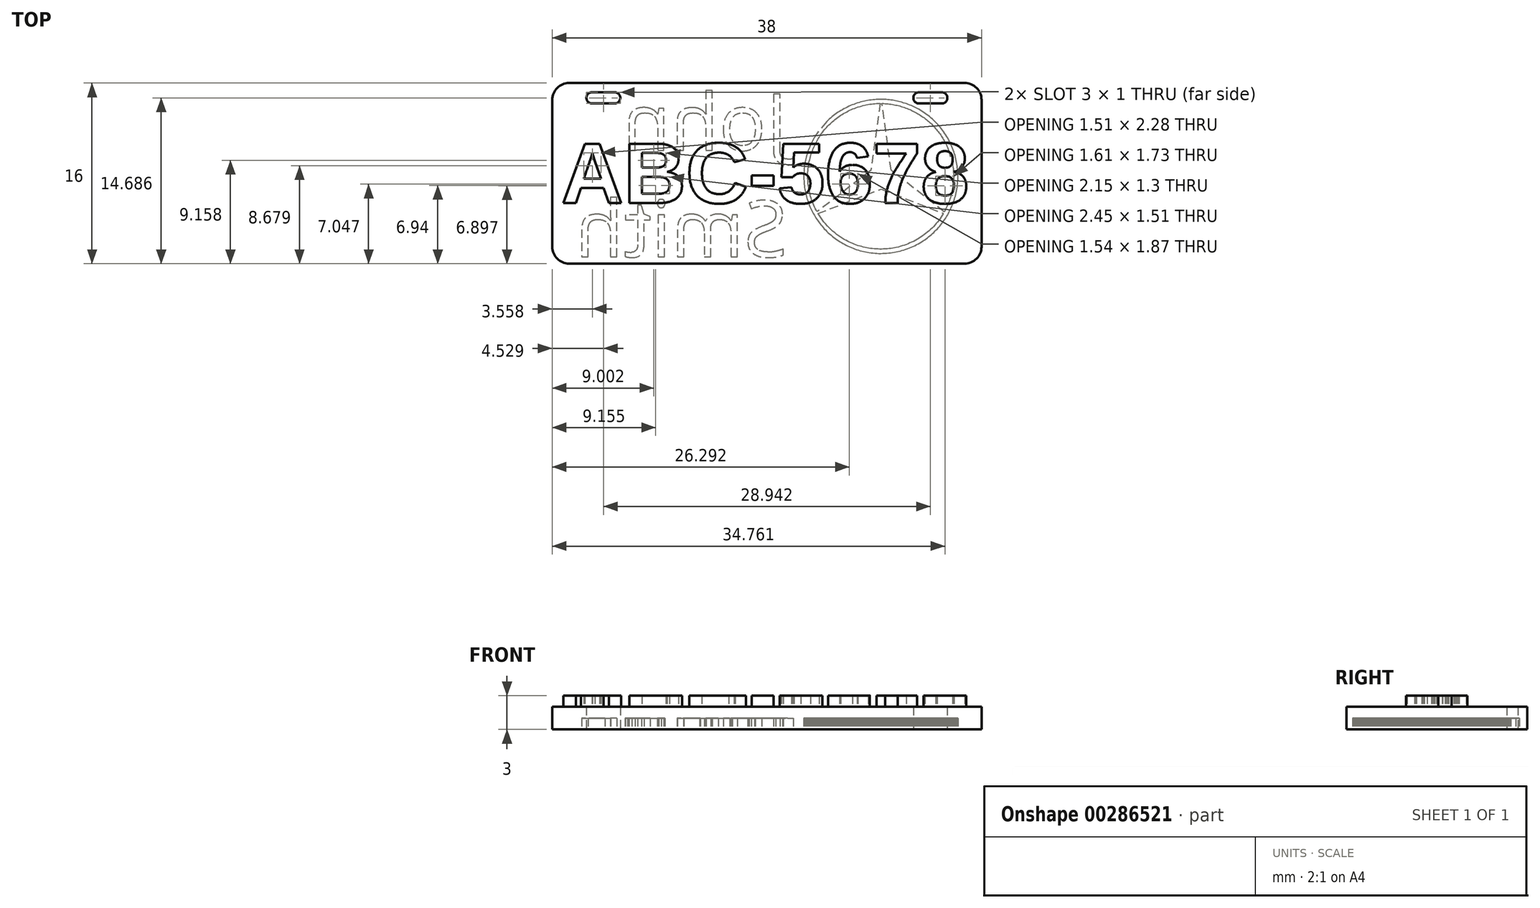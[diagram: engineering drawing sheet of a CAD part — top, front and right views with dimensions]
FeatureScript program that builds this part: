
annotation { "Feature Type Name" : "Feature", "Feature Type Description" : "" }
export const myFeature = defineFeature(function(context is Context, id is Id, definition is map)
    precondition{}
    {
        {
            var Q0;
            Q0=qCreatedBy(makeId("Top.planeOp"),FACE);
            var sketch = newSketch(context, id + "F0", { "sketchPlane" : qUnion([Q0])});
            skLineSegment(sketch, "E0.bottom", {"start": v(1.5, 0) * mm, "end": v(36.5, 0) * mm});
            skLineSegment(sketch, "E0.top", {"start": v(1.5, 16) * mm, "end": v(36.5, 16) * mm});
            skLineSegment(sketch, "E0.left", {"start": v(0, 1.5) * mm, "end": v(0, 14.5) * mm});
            skLineSegment(sketch, "E0.right", {"start": v(38, 1.5) * mm, "end": v(38, 14.5) * mm});
            skPoint(sketch, "E1.visualSharp", {"position": v(0, 16) * mm});
            skArc(sketch, "E1.filletArc", {"start": v(1.5, 16) * mm, "mid": v(0.44, 15.56) * mm, "end": v(0, 14.5) * mm});
            skPoint(sketch, "E2.visualSharp", {"position": v(38, 16) * mm});
            skArc(sketch, "E2.filletArc", {"start": v(38, 14.5) * mm, "mid": v(37.56, 15.56) * mm, "end": v(36.5, 16) * mm});
            skPoint(sketch, "E3.visualSharp", {"position": v(38, 0) * mm});
            skArc(sketch, "E3.filletArc", {"start": v(36.5, 0) * mm, "mid": v(37.56, 0.44) * mm, "end": v(38, 1.5) * mm});
            skPoint(sketch, "E4.visualSharp", {"position": v(0, 0) * mm});
            skArc(sketch, "E4.filletArc", {"start": v(0, 1.5) * mm, "mid": v(0.44, 0.44) * mm, "end": v(1.5, 0) * mm});
            skSolve(sketch);
        }
        {
            var Q0;
            Q0 = qSketchRegion(id + "F0", true);
            extrude(context, id + "F1", {"entities" : qUnion([Q0]), "depth" : 2 * mm, "offsetDistance" : 25 * mm});
        }
        {
            var Q0;
            Q0=makeQuery(id+"F1.opExtrude","CAP_FACE",FACE,{"disambiguationData":[OSD([sQuery(id+"F0.wireOp",EDGE,"E0.bottom"),sQuery(id+"F0.wireOp",EDGE,"E0.top"),sQuery(id+"F0.wireOp",EDGE,"E0.left"),sQuery(id+"F0.wireOp",EDGE,"E0.right"),sQuery(id+"F0.wireOp",EDGE,"E1.filletArc"),sQuery(id+"F0.wireOp",EDGE,"E2.filletArc"),sQuery(id+"F0.wireOp",EDGE,"E3.filletArc"),sQuery(id+"F0.wireOp",EDGE,"E4.filletArc")])],"isStart":false});
            var sketch = newSketch(context, id + "F2", { "sketchPlane" : qUnion([Q0])});
            skPoint(sketch, "E5", {"position": v(19, 16) * mm});
            skText(sketch, "E6", { "text": "ABC-5678", "fontName": "Arimo-Bold.ttf"});
            const initialGuessF2  = {"E6": [0.0008, 0.00537, 1, 0, 0.0055]};
            skSetInitialGuess(sketch, initialGuessF2);
            skSolve(sketch);
        }
        {
            var Q0;
            Q0 = qSketchRegion(id + "F2", true);
            extrude(context, id + "F3", {"entities" : qUnion([Q0]), "depth" : 1 * mm, "offsetDistance" : 25 * mm});
        }
        {
            var Q0;
            Q0=makeQuery(id+"F1.opExtrude","CAP_FACE",FACE,{"disambiguationData":[OSD([sQuery(id+"F0.wireOp",EDGE,"E0.bottom"),sQuery(id+"F0.wireOp",EDGE,"E0.top"),sQuery(id+"F0.wireOp",EDGE,"E0.left"),sQuery(id+"F0.wireOp",EDGE,"E0.right"),sQuery(id+"F0.wireOp",EDGE,"E1.filletArc"),sQuery(id+"F0.wireOp",EDGE,"E2.filletArc"),sQuery(id+"F0.wireOp",EDGE,"E3.filletArc"),sQuery(id+"F0.wireOp",EDGE,"E4.filletArc")])],"isStart":true});
            var sketch = newSketch(context, id + "F4", { "sketchPlane" : qUnion([Q0])});
            skLineSegment(sketch, "E7", {"start": v(32.84, -2.03) * mm, "end": v(32.96, -2.12) * mm});
            skLineSegment(sketch, "E8", {"start": v(32.96, -2.12) * mm, "end": v(33.09, -2.2) * mm});
            skLineSegment(sketch, "E9", {"start": v(33.09, -2.2) * mm, "end": v(33.2, -2.3) * mm});
            skLineSegment(sketch, "E10", {"start": v(33.2, -2.3) * mm, "end": v(33.32, -2.38) * mm});
            skLineSegment(sketch, "E11", {"start": v(33.32, -2.38) * mm, "end": v(33.44, -2.48) * mm});
            skLineSegment(sketch, "E12", {"start": v(33.44, -2.48) * mm, "end": v(33.55, -2.57) * mm});
            skLineSegment(sketch, "E13", {"start": v(33.55, -2.57) * mm, "end": v(33.67, -2.67) * mm});
            skLineSegment(sketch, "E14", {"start": v(33.67, -2.67) * mm, "end": v(33.78, -2.78) * mm});
            skLineSegment(sketch, "E15", {"start": v(33.78, -2.78) * mm, "end": v(33.88, -2.88) * mm});
            skLineSegment(sketch, "E16", {"start": v(33.88, -2.88) * mm, "end": v(33.99, -2.99) * mm});
            skLineSegment(sketch, "E17", {"start": v(33.99, -2.99) * mm, "end": v(34.1, -3.1) * mm});
            skLineSegment(sketch, "E18", {"start": v(34.1, -3.1) * mm, "end": v(34.2, -3.2) * mm});
            skLineSegment(sketch, "E19", {"start": v(34.2, -3.2) * mm, "end": v(34.3, -3.32) * mm});
            skLineSegment(sketch, "E20", {"start": v(34.3, -3.32) * mm, "end": v(34.39, -3.44) * mm});
            skLineSegment(sketch, "E21", {"start": v(34.39, -3.44) * mm, "end": v(34.48, -3.55) * mm});
            skLineSegment(sketch, "E22", {"start": v(34.48, -3.55) * mm, "end": v(34.57, -3.67) * mm});
            skLineSegment(sketch, "E23", {"start": v(34.57, -3.67) * mm, "end": v(34.66, -3.8) * mm});
            skLineSegment(sketch, "E24", {"start": v(34.66, -3.8) * mm, "end": v(34.74, -3.92) * mm});
            skLineSegment(sketch, "E25", {"start": v(34.74, -3.92) * mm, "end": v(34.82, -4.04) * mm});
            skLineSegment(sketch, "E26", {"start": v(34.82, -4.04) * mm, "end": v(34.9, -4.17) * mm});
            skLineSegment(sketch, "E27", {"start": v(34.9, -4.17) * mm, "end": v(34.98, -4.3) * mm});
            skLineSegment(sketch, "E28", {"start": v(34.98, -4.3) * mm, "end": v(35.05, -4.43) * mm});
            skLineSegment(sketch, "E29", {"start": v(35.05, -4.43) * mm, "end": v(35.12, -4.56) * mm});
            skLineSegment(sketch, "E30", {"start": v(35.12, -4.56) * mm, "end": v(35.2, -4.7) * mm});
            skLineSegment(sketch, "E31", {"start": v(35.2, -4.7) * mm, "end": v(35.26, -4.83) * mm});
            skLineSegment(sketch, "E32", {"start": v(35.26, -4.83) * mm, "end": v(35.32, -4.97) * mm});
            skLineSegment(sketch, "E33", {"start": v(35.32, -4.97) * mm, "end": v(35.38, -5.1) * mm});
            skLineSegment(sketch, "E34", {"start": v(35.38, -5.1) * mm, "end": v(35.44, -5.24) * mm});
            skLineSegment(sketch, "E35", {"start": v(35.44, -5.24) * mm, "end": v(35.49, -5.38) * mm});
            skLineSegment(sketch, "E36", {"start": v(35.49, -5.38) * mm, "end": v(35.54, -5.53) * mm});
            skLineSegment(sketch, "E37", {"start": v(35.54, -5.53) * mm, "end": v(35.6, -5.68) * mm});
            skLineSegment(sketch, "E38", {"start": v(35.6, -5.68) * mm, "end": v(35.64, -5.83) * mm});
            skLineSegment(sketch, "E39", {"start": v(35.64, -5.83) * mm, "end": v(35.68, -5.99) * mm});
            skLineSegment(sketch, "E40", {"start": v(35.68, -5.99) * mm, "end": v(35.72, -6.14) * mm});
            skLineSegment(sketch, "E41", {"start": v(35.72, -6.14) * mm, "end": v(35.76, -6.3) * mm});
            skLineSegment(sketch, "E42", {"start": v(35.76, -6.3) * mm, "end": v(35.79, -6.45) * mm});
            skLineSegment(sketch, "E43", {"start": v(35.79, -6.45) * mm, "end": v(35.81, -6.6) * mm});
            skLineSegment(sketch, "E44", {"start": v(35.81, -6.6) * mm, "end": v(35.84, -6.76) * mm});
            skLineSegment(sketch, "E45", {"start": v(35.84, -6.76) * mm, "end": v(35.86, -6.92) * mm});
            skLineSegment(sketch, "E46", {"start": v(35.86, -6.92) * mm, "end": v(35.88, -7.08) * mm});
            skLineSegment(sketch, "E47", {"start": v(35.88, -7.08) * mm, "end": v(35.89, -7.23) * mm});
            skLineSegment(sketch, "E48", {"start": v(35.89, -7.23) * mm, "end": v(35.9, -7.4) * mm});
            skLineSegment(sketch, "E49", {"start": v(35.9, -7.4) * mm, "end": v(35.9, -7.55) * mm});
            skLineSegment(sketch, "E50", {"start": v(35.9, -7.55) * mm, "end": v(35.9, -7.7) * mm});
            skLineSegment(sketch, "E51", {"start": v(35.9, -7.7) * mm, "end": v(35.9, -7.87) * mm});
            skLineSegment(sketch, "E52", {"start": v(35.9, -7.87) * mm, "end": v(35.9, -8.03) * mm});
            skLineSegment(sketch, "E53", {"start": v(35.9, -8.03) * mm, "end": v(35.9, -8.18) * mm});
            skLineSegment(sketch, "E54", {"start": v(35.9, -8.18) * mm, "end": v(35.88, -8.34) * mm});
            skLineSegment(sketch, "E55", {"start": v(35.88, -8.34) * mm, "end": v(35.86, -8.5) * mm});
            skLineSegment(sketch, "E56", {"start": v(35.86, -8.5) * mm, "end": v(35.84, -8.66) * mm});
            skLineSegment(sketch, "E57", {"start": v(35.84, -8.66) * mm, "end": v(35.82, -8.81) * mm});
            skLineSegment(sketch, "E58", {"start": v(35.82, -8.81) * mm, "end": v(35.8, -8.97) * mm});
            skLineSegment(sketch, "E59", {"start": v(35.8, -8.97) * mm, "end": v(35.76, -9.12) * mm});
            skLineSegment(sketch, "E60", {"start": v(35.76, -9.12) * mm, "end": v(35.73, -9.28) * mm});
            skLineSegment(sketch, "E61", {"start": v(35.73, -9.28) * mm, "end": v(35.69, -9.43) * mm});
            skLineSegment(sketch, "E62", {"start": v(35.69, -9.43) * mm, "end": v(35.65, -9.58) * mm});
            skLineSegment(sketch, "E63", {"start": v(35.65, -9.58) * mm, "end": v(35.6, -9.74) * mm});
            skLineSegment(sketch, "E64", {"start": v(35.6, -9.74) * mm, "end": v(35.55, -9.89) * mm});
            skLineSegment(sketch, "E65", {"start": v(35.55, -9.89) * mm, "end": v(35.5, -10.05) * mm});
            skLineSegment(sketch, "E66", {"start": v(35.5, -10.05) * mm, "end": v(35.44, -10.2) * mm});
            skLineSegment(sketch, "E67", {"start": v(35.44, -10.2) * mm, "end": v(35.38, -10.36) * mm});
            skLineSegment(sketch, "E68", {"start": v(35.38, -10.36) * mm, "end": v(35.31, -10.51) * mm});
            skLineSegment(sketch, "E69", {"start": v(35.31, -10.51) * mm, "end": v(35.24, -10.66) * mm});
            skLineSegment(sketch, "E70", {"start": v(35.24, -10.66) * mm, "end": v(35.17, -10.82) * mm});
            skLineSegment(sketch, "E71", {"start": v(35.17, -10.82) * mm, "end": v(35.1, -10.96) * mm});
            skLineSegment(sketch, "E72", {"start": v(35.1, -10.96) * mm, "end": v(35.01, -11.1) * mm});
            skLineSegment(sketch, "E73", {"start": v(35.01, -11.1) * mm, "end": v(34.93, -11.25) * mm});
            skLineSegment(sketch, "E74", {"start": v(34.93, -11.25) * mm, "end": v(34.84, -11.4) * mm});
            skLineSegment(sketch, "E75", {"start": v(34.84, -11.4) * mm, "end": v(34.75, -11.54) * mm});
            skLineSegment(sketch, "E76", {"start": v(34.75, -11.54) * mm, "end": v(34.65, -11.67) * mm});
            skLineSegment(sketch, "E77", {"start": v(34.65, -11.67) * mm, "end": v(34.55, -11.8) * mm});
            skLineSegment(sketch, "E78", {"start": v(34.55, -11.8) * mm, "end": v(34.45, -11.94) * mm});
            skLineSegment(sketch, "E79", {"start": v(34.45, -11.94) * mm, "end": v(34.34, -12.07) * mm});
            skLineSegment(sketch, "E80", {"start": v(34.34, -12.07) * mm, "end": v(34.24, -12.2) * mm});
            skLineSegment(sketch, "E81", {"start": v(34.24, -12.2) * mm, "end": v(34.12, -12.32) * mm});
            skLineSegment(sketch, "E82", {"start": v(34.12, -12.32) * mm, "end": v(34.01, -12.45) * mm});
            skLineSegment(sketch, "E83", {"start": v(34.01, -12.45) * mm, "end": v(33.9, -12.57) * mm});
            skLineSegment(sketch, "E84", {"start": v(33.9, -12.57) * mm, "end": v(33.77, -12.68) * mm});
            skLineSegment(sketch, "E85", {"start": v(33.77, -12.68) * mm, "end": v(33.65, -12.8) * mm});
            skLineSegment(sketch, "E86", {"start": v(33.65, -12.8) * mm, "end": v(33.52, -12.9) * mm});
            skLineSegment(sketch, "E87", {"start": v(33.52, -12.9) * mm, "end": v(33.4, -13.01) * mm});
            skLineSegment(sketch, "E88", {"start": v(33.4, -13.01) * mm, "end": v(33.27, -13.12) * mm});
            skLineSegment(sketch, "E89", {"start": v(33.27, -13.12) * mm, "end": v(33.13, -13.22) * mm});
            skLineSegment(sketch, "E90", {"start": v(33.13, -13.22) * mm, "end": v(33, -13.32) * mm});
            skLineSegment(sketch, "E91", {"start": v(33, -13.32) * mm, "end": v(32.86, -13.41) * mm});
            skLineSegment(sketch, "E92", {"start": v(32.86, -13.41) * mm, "end": v(32.72, -13.5) * mm});
            skLineSegment(sketch, "E93", {"start": v(32.72, -13.5) * mm, "end": v(32.57, -13.6) * mm});
            skLineSegment(sketch, "E94", {"start": v(32.57, -13.6) * mm, "end": v(32.42, -13.68) * mm});
            skLineSegment(sketch, "E95", {"start": v(32.42, -13.68) * mm, "end": v(32.3, -13.75) * mm});
            skLineSegment(sketch, "E96", {"start": v(32.3, -13.75) * mm, "end": v(32.17, -13.81) * mm});
            skLineSegment(sketch, "E97", {"start": v(32.17, -13.81) * mm, "end": v(32.04, -13.88) * mm});
            skLineSegment(sketch, "E98", {"start": v(32.04, -13.88) * mm, "end": v(31.9, -13.94) * mm});
            skLineSegment(sketch, "E99", {"start": v(31.9, -13.94) * mm, "end": v(31.78, -14) * mm});
            skLineSegment(sketch, "E100", {"start": v(31.78, -14) * mm, "end": v(31.64, -14.05) * mm});
            skLineSegment(sketch, "E101", {"start": v(31.64, -14.05) * mm, "end": v(31.5, -14.1) * mm});
            skLineSegment(sketch, "E102", {"start": v(31.5, -14.1) * mm, "end": v(31.37, -14.15) * mm});
            skLineSegment(sketch, "E103", {"start": v(31.37, -14.15) * mm, "end": v(31.24, -14.2) * mm});
            skLineSegment(sketch, "E104", {"start": v(31.24, -14.2) * mm, "end": v(31.1, -14.24) * mm});
            skLineSegment(sketch, "E105", {"start": v(31.1, -14.24) * mm, "end": v(30.96, -14.28) * mm});
            skLineSegment(sketch, "E106", {"start": v(30.96, -14.28) * mm, "end": v(30.82, -14.32) * mm});
            skLineSegment(sketch, "E107", {"start": v(30.82, -14.32) * mm, "end": v(30.68, -14.36) * mm});
            skLineSegment(sketch, "E108", {"start": v(30.68, -14.36) * mm, "end": v(30.54, -14.4) * mm});
            skLineSegment(sketch, "E109", {"start": v(30.54, -14.4) * mm, "end": v(30.4, -14.42) * mm});
            skLineSegment(sketch, "E110", {"start": v(30.4, -14.42) * mm, "end": v(30.26, -14.45) * mm});
            skLineSegment(sketch, "E111", {"start": v(30.26, -14.45) * mm, "end": v(30.12, -14.47) * mm});
            skLineSegment(sketch, "E112", {"start": v(30.12, -14.47) * mm, "end": v(29.98, -14.5) * mm});
            skLineSegment(sketch, "E113", {"start": v(29.98, -14.5) * mm, "end": v(29.84, -14.5) * mm});
            skLineSegment(sketch, "E114", {"start": v(29.84, -14.5) * mm, "end": v(29.7, -14.52) * mm});
            skLineSegment(sketch, "E115", {"start": v(29.7, -14.52) * mm, "end": v(29.55, -14.53) * mm});
            skLineSegment(sketch, "E116", {"start": v(29.55, -14.53) * mm, "end": v(29.4, -14.54) * mm});
            skLineSegment(sketch, "E117", {"start": v(29.4, -14.54) * mm, "end": v(29.26, -14.55) * mm});
            skLineSegment(sketch, "E118", {"start": v(29.26, -14.55) * mm, "end": v(29.12, -14.55) * mm});
            skLineSegment(sketch, "E119", {"start": v(29.12, -14.55) * mm, "end": v(28.97, -14.55) * mm});
            skLineSegment(sketch, "E120", {"start": v(28.97, -14.55) * mm, "end": v(28.83, -14.54) * mm});
            skLineSegment(sketch, "E121", {"start": v(28.83, -14.54) * mm, "end": v(28.69, -14.54) * mm});
            skLineSegment(sketch, "E122", {"start": v(28.69, -14.54) * mm, "end": v(28.54, -14.53) * mm});
            skLineSegment(sketch, "E123", {"start": v(28.54, -14.53) * mm, "end": v(28.4, -14.51) * mm});
            skLineSegment(sketch, "E124", {"start": v(28.4, -14.51) * mm, "end": v(28.24, -14.5) * mm});
            skLineSegment(sketch, "E125", {"start": v(28.24, -14.5) * mm, "end": v(28.08, -14.47) * mm});
            skLineSegment(sketch, "E126", {"start": v(28.08, -14.47) * mm, "end": v(27.93, -14.45) * mm});
            skLineSegment(sketch, "E127", {"start": v(27.93, -14.45) * mm, "end": v(27.77, -14.42) * mm});
            skLineSegment(sketch, "E128", {"start": v(27.77, -14.42) * mm, "end": v(27.61, -14.39) * mm});
            skLineSegment(sketch, "E129", {"start": v(27.61, -14.39) * mm, "end": v(27.46, -14.35) * mm});
            skLineSegment(sketch, "E130", {"start": v(27.46, -14.35) * mm, "end": v(27.3, -14.31) * mm});
            skLineSegment(sketch, "E131", {"start": v(27.3, -14.31) * mm, "end": v(27.15, -14.27) * mm});
            skLineSegment(sketch, "E132", {"start": v(27.15, -14.27) * mm, "end": v(27, -14.22) * mm});
            skLineSegment(sketch, "E133", {"start": v(27, -14.22) * mm, "end": v(26.85, -14.17) * mm});
            skLineSegment(sketch, "E134", {"start": v(26.85, -14.17) * mm, "end": v(26.7, -14.11) * mm});
            skLineSegment(sketch, "E135", {"start": v(26.7, -14.11) * mm, "end": v(26.55, -14.06) * mm});
            skLineSegment(sketch, "E136", {"start": v(26.55, -14.06) * mm, "end": v(26.4, -14) * mm});
            skLineSegment(sketch, "E137", {"start": v(26.4, -14) * mm, "end": v(26.25, -13.93) * mm});
            skLineSegment(sketch, "E138", {"start": v(26.25, -13.93) * mm, "end": v(26.1, -13.86) * mm});
            skLineSegment(sketch, "E139", {"start": v(26.1, -13.86) * mm, "end": v(25.97, -13.8) * mm});
            skLineSegment(sketch, "E140", {"start": v(25.97, -13.8) * mm, "end": v(25.83, -13.72) * mm});
            skLineSegment(sketch, "E141", {"start": v(25.83, -13.72) * mm, "end": v(25.69, -13.64) * mm});
            skLineSegment(sketch, "E142", {"start": v(25.69, -13.64) * mm, "end": v(25.55, -13.56) * mm});
            skLineSegment(sketch, "E143", {"start": v(25.55, -13.56) * mm, "end": v(25.41, -13.48) * mm});
            skLineSegment(sketch, "E144", {"start": v(25.41, -13.48) * mm, "end": v(25.28, -13.39) * mm});
            skLineSegment(sketch, "E145", {"start": v(25.28, -13.39) * mm, "end": v(25.15, -13.3) * mm});
            skLineSegment(sketch, "E146", {"start": v(25.15, -13.3) * mm, "end": v(25.02, -13.2) * mm});
            skLineSegment(sketch, "E147", {"start": v(25.02, -13.2) * mm, "end": v(24.9, -13.1) * mm});
            skLineSegment(sketch, "E148", {"start": v(24.9, -13.1) * mm, "end": v(24.77, -13) * mm});
            skLineSegment(sketch, "E149", {"start": v(24.77, -13) * mm, "end": v(24.65, -12.9) * mm});
            skLineSegment(sketch, "E150", {"start": v(24.65, -12.9) * mm, "end": v(24.53, -12.8) * mm});
            skLineSegment(sketch, "E151", {"start": v(24.53, -12.8) * mm, "end": v(24.4, -12.7) * mm});
            skLineSegment(sketch, "E152", {"start": v(24.4, -12.7) * mm, "end": v(24.3, -12.58) * mm});
            skLineSegment(sketch, "E153", {"start": v(24.3, -12.58) * mm, "end": v(23.55, -11.71) * mm});
            skLineSegment(sketch, "E154", {"start": v(23.55, -11.71) * mm, "end": v(23.22, -11.21) * mm});
            skLineSegment(sketch, "E155", {"start": v(23.22, -11.21) * mm, "end": v(23.12, -11.04) * mm});
            skLineSegment(sketch, "E156", {"start": v(23.12, -11.04) * mm, "end": v(23.05, -10.9) * mm});
            skLineSegment(sketch, "E157", {"start": v(23.05, -10.9) * mm, "end": v(22.99, -10.78) * mm});
            skLineSegment(sketch, "E158", {"start": v(22.99, -10.78) * mm, "end": v(22.92, -10.65) * mm});
            skLineSegment(sketch, "E159", {"start": v(22.92, -10.65) * mm, "end": v(22.87, -10.52) * mm});
            skLineSegment(sketch, "E160", {"start": v(22.87, -10.52) * mm, "end": v(22.8, -10.4) * mm});
            skLineSegment(sketch, "E161", {"start": v(22.8, -10.4) * mm, "end": v(22.75, -10.26) * mm});
            skLineSegment(sketch, "E162", {"start": v(22.75, -10.26) * mm, "end": v(22.7, -10.13) * mm});
            skLineSegment(sketch, "E163", {"start": v(22.7, -10.13) * mm, "end": v(22.65, -10) * mm});
            skLineSegment(sketch, "E164", {"start": v(22.65, -10) * mm, "end": v(22.6, -9.86) * mm});
            skLineSegment(sketch, "E165", {"start": v(22.6, -9.86) * mm, "end": v(22.57, -9.72) * mm});
            skLineSegment(sketch, "E166", {"start": v(22.57, -9.72) * mm, "end": v(22.52, -9.58) * mm});
            skLineSegment(sketch, "E167", {"start": v(22.52, -9.58) * mm, "end": v(22.49, -9.45) * mm});
            skLineSegment(sketch, "E168", {"start": v(22.49, -9.45) * mm, "end": v(22.45, -9.3) * mm});
            skLineSegment(sketch, "E169", {"start": v(22.45, -9.3) * mm, "end": v(22.42, -9.17) * mm});
            skLineSegment(sketch, "E170", {"start": v(22.42, -9.17) * mm, "end": v(22.4, -9.03) * mm});
            skLineSegment(sketch, "E171", {"start": v(22.4, -9.03) * mm, "end": v(22.37, -8.89) * mm});
            skLineSegment(sketch, "E172", {"start": v(22.37, -8.89) * mm, "end": v(22.34, -8.75) * mm});
            skLineSegment(sketch, "E173", {"start": v(22.34, -8.75) * mm, "end": v(22.32, -8.6) * mm});
            skLineSegment(sketch, "E174", {"start": v(22.32, -8.6) * mm, "end": v(22.3, -8.46) * mm});
            skLineSegment(sketch, "E175", {"start": v(22.3, -8.46) * mm, "end": v(22.3, -8.32) * mm});
            skLineSegment(sketch, "E176", {"start": v(22.3, -8.32) * mm, "end": v(22.28, -8.18) * mm});
            skLineSegment(sketch, "E177", {"start": v(22.28, -8.18) * mm, "end": v(22.27, -8.04) * mm});
            skLineSegment(sketch, "E178", {"start": v(22.27, -8.04) * mm, "end": v(22.27, -7.9) * mm});
            skLineSegment(sketch, "E179", {"start": v(22.27, -7.9) * mm, "end": v(22.27, -7.75) * mm});
            skLineSegment(sketch, "E180", {"start": v(22.27, -7.75) * mm, "end": v(22.27, -7.6) * mm});
            skLineSegment(sketch, "E181", {"start": v(22.27, -7.6) * mm, "end": v(22.27, -7.47) * mm});
            skLineSegment(sketch, "E182", {"start": v(22.27, -7.47) * mm, "end": v(22.28, -7.32) * mm});
            skLineSegment(sketch, "E183", {"start": v(22.28, -7.32) * mm, "end": v(22.29, -7.18) * mm});
            skLineSegment(sketch, "E184", {"start": v(22.29, -7.18) * mm, "end": v(22.3, -7.04) * mm});
            skLineSegment(sketch, "E185", {"start": v(22.3, -7.04) * mm, "end": v(22.32, -6.9) * mm});
            skLineSegment(sketch, "E186", {"start": v(22.32, -6.9) * mm, "end": v(22.34, -6.75) * mm});
            skLineSegment(sketch, "E187", {"start": v(22.34, -6.75) * mm, "end": v(22.36, -6.6) * mm});
            skLineSegment(sketch, "E188", {"start": v(22.36, -6.6) * mm, "end": v(22.39, -6.46) * mm});
            skLineSegment(sketch, "E189", {"start": v(22.39, -6.46) * mm, "end": v(22.41, -6.32) * mm});
            skLineSegment(sketch, "E190", {"start": v(22.41, -6.32) * mm, "end": v(22.45, -6.18) * mm});
            skLineSegment(sketch, "E191", {"start": v(22.45, -6.18) * mm, "end": v(22.48, -6.03) * mm});
            skLineSegment(sketch, "E192", {"start": v(22.48, -6.03) * mm, "end": v(22.52, -5.9) * mm});
            skLineSegment(sketch, "E193", {"start": v(22.52, -5.9) * mm, "end": v(22.56, -5.75) * mm});
            skLineSegment(sketch, "E194", {"start": v(22.56, -5.75) * mm, "end": v(22.6, -5.61) * mm});
            skLineSegment(sketch, "E195", {"start": v(22.6, -5.61) * mm, "end": v(22.65, -5.47) * mm});
            skLineSegment(sketch, "E196", {"start": v(22.65, -5.47) * mm, "end": v(22.7, -5.34) * mm});
            skLineSegment(sketch, "E197", {"start": v(22.7, -5.34) * mm, "end": v(22.75, -5.2) * mm});
            skLineSegment(sketch, "E198", {"start": v(22.75, -5.2) * mm, "end": v(22.8, -5.07) * mm});
            skLineSegment(sketch, "E199", {"start": v(22.8, -5.07) * mm, "end": v(22.87, -4.93) * mm});
            skLineSegment(sketch, "E200", {"start": v(22.87, -4.93) * mm, "end": v(22.93, -4.8) * mm});
            skLineSegment(sketch, "E201", {"start": v(22.93, -4.8) * mm, "end": v(23, -4.67) * mm});
            skLineSegment(sketch, "E202", {"start": v(23, -4.67) * mm, "end": v(23.06, -4.54) * mm});
            skLineSegment(sketch, "E203", {"start": v(23.06, -4.54) * mm, "end": v(23.13, -4.4) * mm});
            skLineSegment(sketch, "E204", {"start": v(23.13, -4.4) * mm, "end": v(23.2, -4.28) * mm});
            skLineSegment(sketch, "E205", {"start": v(23.2, -4.28) * mm, "end": v(23.28, -4.16) * mm});
            skLineSegment(sketch, "E206", {"start": v(23.28, -4.16) * mm, "end": v(23.35, -4.03) * mm});
            skLineSegment(sketch, "E207", {"start": v(23.35, -4.03) * mm, "end": v(23.43, -3.91) * mm});
            skLineSegment(sketch, "E208", {"start": v(23.43, -3.91) * mm, "end": v(23.52, -3.8) * mm});
            skLineSegment(sketch, "E209", {"start": v(23.52, -3.8) * mm, "end": v(23.6, -3.67) * mm});
            skLineSegment(sketch, "E210", {"start": v(23.6, -3.67) * mm, "end": v(23.7, -3.56) * mm});
            skLineSegment(sketch, "E211", {"start": v(23.7, -3.56) * mm, "end": v(23.78, -3.44) * mm});
            skLineSegment(sketch, "E212", {"start": v(23.78, -3.44) * mm, "end": v(23.87, -3.33) * mm});
            skLineSegment(sketch, "E213", {"start": v(23.87, -3.33) * mm, "end": v(23.97, -3.22) * mm});
            skLineSegment(sketch, "E214", {"start": v(23.97, -3.22) * mm, "end": v(24.08, -3.1) * mm});
            skLineSegment(sketch, "E215", {"start": v(24.08, -3.1) * mm, "end": v(24.2, -2.98) * mm});
            skLineSegment(sketch, "E216", {"start": v(24.2, -2.98) * mm, "end": v(24.3, -2.86) * mm});
            skLineSegment(sketch, "E217", {"start": v(24.3, -2.86) * mm, "end": v(24.43, -2.75) * mm});
            skLineSegment(sketch, "E218", {"start": v(24.43, -2.75) * mm, "end": v(24.55, -2.64) * mm});
            skLineSegment(sketch, "E219", {"start": v(24.55, -2.64) * mm, "end": v(24.67, -2.53) * mm});
            skLineSegment(sketch, "E220", {"start": v(24.67, -2.53) * mm, "end": v(24.8, -2.43) * mm});
            skLineSegment(sketch, "E221", {"start": v(24.8, -2.43) * mm, "end": v(24.93, -2.33) * mm});
            skLineSegment(sketch, "E222", {"start": v(24.93, -2.33) * mm, "end": v(25.06, -2.23) * mm});
            skLineSegment(sketch, "E223", {"start": v(25.06, -2.23) * mm, "end": v(25.19, -2.13) * mm});
            skLineSegment(sketch, "E224", {"start": v(25.19, -2.13) * mm, "end": v(25.33, -2.04) * mm});
            skLineSegment(sketch, "E225", {"start": v(25.33, -2.04) * mm, "end": v(25.46, -1.95) * mm});
            skLineSegment(sketch, "E226", {"start": v(25.46, -1.95) * mm, "end": v(25.6, -1.87) * mm});
            skLineSegment(sketch, "E227", {"start": v(25.6, -1.87) * mm, "end": v(25.74, -1.79) * mm});
            skLineSegment(sketch, "E228", {"start": v(25.74, -1.79) * mm, "end": v(25.89, -1.7) * mm});
            skLineSegment(sketch, "E229", {"start": v(25.89, -1.7) * mm, "end": v(26.03, -1.63) * mm});
            skLineSegment(sketch, "E230", {"start": v(26.03, -1.63) * mm, "end": v(26.18, -1.56) * mm});
            skLineSegment(sketch, "E231", {"start": v(26.18, -1.56) * mm, "end": v(26.33, -1.5) * mm});
            skLineSegment(sketch, "E232", {"start": v(26.33, -1.5) * mm, "end": v(26.48, -1.43) * mm});
            skLineSegment(sketch, "E233", {"start": v(26.48, -1.43) * mm, "end": v(26.63, -1.37) * mm});
            skLineSegment(sketch, "E234", {"start": v(26.63, -1.37) * mm, "end": v(26.78, -1.3) * mm});
            skLineSegment(sketch, "E235", {"start": v(26.78, -1.3) * mm, "end": v(26.94, -1.26) * mm});
            skLineSegment(sketch, "E236", {"start": v(26.94, -1.26) * mm, "end": v(27.1, -1.2) * mm});
            skLineSegment(sketch, "E237", {"start": v(27.1, -1.2) * mm, "end": v(27.25, -1.16) * mm});
            skLineSegment(sketch, "E238", {"start": v(27.25, -1.16) * mm, "end": v(27.41, -1.12) * mm});
            skLineSegment(sketch, "E239", {"start": v(27.41, -1.12) * mm, "end": v(27.57, -1.08) * mm});
            skLineSegment(sketch, "E240", {"start": v(27.57, -1.08) * mm, "end": v(27.73, -1.04) * mm});
            skLineSegment(sketch, "E241", {"start": v(27.73, -1.04) * mm, "end": v(27.9, -1.01) * mm});
            skLineSegment(sketch, "E242", {"start": v(27.9, -1.01) * mm, "end": v(28.05, -0.99) * mm});
            skLineSegment(sketch, "E243", {"start": v(28.05, -0.99) * mm, "end": v(28.22, -0.96) * mm});
            skLineSegment(sketch, "E244", {"start": v(28.22, -0.96) * mm, "end": v(28.4, -0.94) * mm});
            skLineSegment(sketch, "E245", {"start": v(28.4, -0.94) * mm, "end": v(28.57, -0.93) * mm});
            skLineSegment(sketch, "E246", {"start": v(28.57, -0.93) * mm, "end": v(28.74, -0.92) * mm});
            skLineSegment(sketch, "E247", {"start": v(28.74, -0.92) * mm, "end": v(28.91, -0.9) * mm});
            skLineSegment(sketch, "E248", {"start": v(28.91, -0.9) * mm, "end": v(29.08, -0.9) * mm});
            skLineSegment(sketch, "E249", {"start": v(29.08, -0.9) * mm, "end": v(29.26, -0.91) * mm});
            skLineSegment(sketch, "E250", {"start": v(29.26, -0.91) * mm, "end": v(29.43, -0.92) * mm});
            skLineSegment(sketch, "E251", {"start": v(29.43, -0.92) * mm, "end": v(29.6, -0.93) * mm});
            skLineSegment(sketch, "E252", {"start": v(29.6, -0.93) * mm, "end": v(29.77, -0.94) * mm});
            skLineSegment(sketch, "E253", {"start": v(29.77, -0.94) * mm, "end": v(29.95, -0.96) * mm});
            skLineSegment(sketch, "E254", {"start": v(29.95, -0.96) * mm, "end": v(30.12, -0.99) * mm});
            skLineSegment(sketch, "E255", {"start": v(30.12, -0.99) * mm, "end": v(30.29, -1.02) * mm});
            skLineSegment(sketch, "E256", {"start": v(30.29, -1.02) * mm, "end": v(30.46, -1.05) * mm});
            skLineSegment(sketch, "E257", {"start": v(30.46, -1.05) * mm, "end": v(30.63, -1.09) * mm});
            skLineSegment(sketch, "E258", {"start": v(30.63, -1.09) * mm, "end": v(30.8, -1.13) * mm});
            skLineSegment(sketch, "E259", {"start": v(30.8, -1.13) * mm, "end": v(30.96, -1.17) * mm});
            skLineSegment(sketch, "E260", {"start": v(30.96, -1.17) * mm, "end": v(31.13, -1.22) * mm});
            skLineSegment(sketch, "E261", {"start": v(31.13, -1.22) * mm, "end": v(31.3, -1.28) * mm});
            skLineSegment(sketch, "E262", {"start": v(31.3, -1.28) * mm, "end": v(31.45, -1.33) * mm});
            skLineSegment(sketch, "E263", {"start": v(31.45, -1.33) * mm, "end": v(31.61, -1.4) * mm});
            skLineSegment(sketch, "E264", {"start": v(31.61, -1.4) * mm, "end": v(31.77, -1.46) * mm});
            skLineSegment(sketch, "E265", {"start": v(31.77, -1.46) * mm, "end": v(31.93, -1.53) * mm});
            skLineSegment(sketch, "E266", {"start": v(31.93, -1.53) * mm, "end": v(32.09, -1.6) * mm});
            skLineSegment(sketch, "E267", {"start": v(32.09, -1.6) * mm, "end": v(32.24, -1.68) * mm});
            skLineSegment(sketch, "E268", {"start": v(32.24, -1.68) * mm, "end": v(32.4, -1.76) * mm});
            skLineSegment(sketch, "E269", {"start": v(32.4, -1.76) * mm, "end": v(32.54, -1.85) * mm});
            skLineSegment(sketch, "E270", {"start": v(32.54, -1.85) * mm, "end": v(32.7, -1.94) * mm});
            skLineSegment(sketch, "E271", {"start": v(32.7, -1.94) * mm, "end": v(32.84, -2.03) * mm});
            skLineSegment(sketch, "E272", {"start": v(30.46, -1.44) * mm, "end": v(30.3, -1.4) * mm});
            skLineSegment(sketch, "E273", {"start": v(30.3, -1.4) * mm, "end": v(30.14, -1.38) * mm});
            skLineSegment(sketch, "E274", {"start": v(30.14, -1.38) * mm, "end": v(29.97, -1.35) * mm});
            skLineSegment(sketch, "E275", {"start": v(29.97, -1.35) * mm, "end": v(29.81, -1.33) * mm});
            skLineSegment(sketch, "E276", {"start": v(29.81, -1.33) * mm, "end": v(29.65, -1.31) * mm});
            skLineSegment(sketch, "E277", {"start": v(29.65, -1.31) * mm, "end": v(29.48, -1.3) * mm});
            skLineSegment(sketch, "E278", {"start": v(29.48, -1.3) * mm, "end": v(29.32, -1.3) * mm});
            skLineSegment(sketch, "E279", {"start": v(29.32, -1.3) * mm, "end": v(29.16, -1.29) * mm});
            skLineSegment(sketch, "E280", {"start": v(29.16, -1.29) * mm, "end": v(29, -1.29) * mm});
            skLineSegment(sketch, "E281", {"start": v(29, -1.29) * mm, "end": v(28.83, -1.3) * mm});
            skLineSegment(sketch, "E282", {"start": v(28.83, -1.3) * mm, "end": v(28.67, -1.3) * mm});
            skLineSegment(sketch, "E283", {"start": v(28.67, -1.3) * mm, "end": v(28.5, -1.31) * mm});
            skLineSegment(sketch, "E284", {"start": v(28.5, -1.31) * mm, "end": v(28.34, -1.33) * mm});
            skLineSegment(sketch, "E285", {"start": v(28.34, -1.33) * mm, "end": v(28.18, -1.35) * mm});
            skLineSegment(sketch, "E286", {"start": v(28.18, -1.35) * mm, "end": v(28.01, -1.37) * mm});
            skLineSegment(sketch, "E287", {"start": v(28.01, -1.37) * mm, "end": v(27.85, -1.4) * mm});
            skLineSegment(sketch, "E288", {"start": v(27.85, -1.4) * mm, "end": v(27.7, -1.44) * mm});
            skLineSegment(sketch, "E289", {"start": v(27.7, -1.44) * mm, "end": v(27.53, -1.47) * mm});
            skLineSegment(sketch, "E290", {"start": v(27.53, -1.47) * mm, "end": v(27.37, -1.51) * mm});
            skLineSegment(sketch, "E291", {"start": v(27.37, -1.51) * mm, "end": v(27.22, -1.56) * mm});
            skLineSegment(sketch, "E292", {"start": v(27.22, -1.56) * mm, "end": v(27.06, -1.6) * mm});
            skLineSegment(sketch, "E293", {"start": v(27.06, -1.6) * mm, "end": v(26.9, -1.66) * mm});
            skLineSegment(sketch, "E294", {"start": v(26.9, -1.66) * mm, "end": v(26.75, -1.72) * mm});
            skLineSegment(sketch, "E295", {"start": v(26.75, -1.72) * mm, "end": v(26.6, -1.78) * mm});
            skLineSegment(sketch, "E296", {"start": v(26.6, -1.78) * mm, "end": v(26.45, -1.84) * mm});
            skLineSegment(sketch, "E297", {"start": v(26.45, -1.84) * mm, "end": v(26.3, -1.91) * mm});
            skLineSegment(sketch, "E298", {"start": v(26.3, -1.91) * mm, "end": v(26.15, -1.98) * mm});
            skLineSegment(sketch, "E299", {"start": v(26.15, -1.98) * mm, "end": v(26, -2.06) * mm});
            skLineSegment(sketch, "E300", {"start": v(26, -2.06) * mm, "end": v(25.87, -2.14) * mm});
            skLineSegment(sketch, "E301", {"start": v(25.87, -2.14) * mm, "end": v(25.77, -2.2) * mm});
            skLineSegment(sketch, "E302", {"start": v(25.77, -2.2) * mm, "end": v(25.57, -2.32) * mm});
            skLineSegment(sketch, "E303", {"start": v(25.57, -2.32) * mm, "end": v(25.38, -2.45) * mm});
            skLineSegment(sketch, "E304", {"start": v(25.38, -2.45) * mm, "end": v(25.2, -2.58) * mm});
            skLineSegment(sketch, "E305", {"start": v(25.2, -2.58) * mm, "end": v(25.01, -2.72) * mm});
            skLineSegment(sketch, "E306", {"start": v(25.01, -2.72) * mm, "end": v(24.84, -2.87) * mm});
            skLineSegment(sketch, "E307", {"start": v(24.84, -2.87) * mm, "end": v(24.67, -3.02) * mm});
            skLineSegment(sketch, "E308", {"start": v(24.67, -3.02) * mm, "end": v(24.5, -3.18) * mm});
            skLineSegment(sketch, "E309", {"start": v(24.5, -3.18) * mm, "end": v(24.35, -3.35) * mm});
            skLineSegment(sketch, "E310", {"start": v(24.35, -3.35) * mm, "end": v(24.2, -3.52) * mm});
            skLineSegment(sketch, "E311", {"start": v(24.2, -3.52) * mm, "end": v(24.05, -3.7) * mm});
            skLineSegment(sketch, "E312", {"start": v(24.05, -3.7) * mm, "end": v(23.9, -3.88) * mm});
            skLineSegment(sketch, "E313", {"start": v(23.9, -3.88) * mm, "end": v(23.77, -4.06) * mm});
            skLineSegment(sketch, "E314", {"start": v(23.77, -4.06) * mm, "end": v(23.64, -4.25) * mm});
            skLineSegment(sketch, "E315", {"start": v(23.64, -4.25) * mm, "end": v(23.52, -4.45) * mm});
            skLineSegment(sketch, "E316", {"start": v(23.52, -4.45) * mm, "end": v(29.12, -6.6) * mm});
            skLineSegment(sketch, "E317", {"start": v(29.12, -6.6) * mm, "end": v(34.62, -4.44) * mm});
            skLineSegment(sketch, "E318", {"start": v(34.62, -4.44) * mm, "end": v(34.53, -4.29) * mm});
            skLineSegment(sketch, "E319", {"start": v(34.53, -4.29) * mm, "end": v(34.43, -4.13) * mm});
            skLineSegment(sketch, "E320", {"start": v(34.43, -4.13) * mm, "end": v(34.32, -3.98) * mm});
            skLineSegment(sketch, "E321", {"start": v(34.32, -3.98) * mm, "end": v(34.22, -3.84) * mm});
            skLineSegment(sketch, "E322", {"start": v(34.22, -3.84) * mm, "end": v(34.1, -3.7) * mm});
            skLineSegment(sketch, "E323", {"start": v(34.1, -3.7) * mm, "end": v(33.99, -3.55) * mm});
            skLineSegment(sketch, "E324", {"start": v(33.99, -3.55) * mm, "end": v(33.87, -3.42) * mm});
            skLineSegment(sketch, "E325", {"start": v(33.87, -3.42) * mm, "end": v(33.74, -3.29) * mm});
            skLineSegment(sketch, "E326", {"start": v(33.74, -3.29) * mm, "end": v(33.62, -3.16) * mm});
            skLineSegment(sketch, "E327", {"start": v(33.62, -3.16) * mm, "end": v(33.48, -3.03) * mm});
            skLineSegment(sketch, "E328", {"start": v(33.48, -3.03) * mm, "end": v(33.35, -2.9) * mm});
            skLineSegment(sketch, "E329", {"start": v(33.35, -2.9) * mm, "end": v(33.21, -2.79) * mm});
            skLineSegment(sketch, "E330", {"start": v(33.21, -2.79) * mm, "end": v(33.07, -2.67) * mm});
            skLineSegment(sketch, "E331", {"start": v(33.07, -2.67) * mm, "end": v(32.92, -2.56) * mm});
            skLineSegment(sketch, "E332", {"start": v(32.92, -2.56) * mm, "end": v(32.78, -2.46) * mm});
            skLineSegment(sketch, "E333", {"start": v(32.78, -2.46) * mm, "end": v(32.63, -2.36) * mm});
            skLineSegment(sketch, "E334", {"start": v(32.63, -2.36) * mm, "end": v(32.47, -2.26) * mm});
            skLineSegment(sketch, "E335", {"start": v(32.47, -2.26) * mm, "end": v(32.32, -2.16) * mm});
            skLineSegment(sketch, "E336", {"start": v(32.32, -2.16) * mm, "end": v(32.16, -2.07) * mm});
            skLineSegment(sketch, "E337", {"start": v(32.16, -2.07) * mm, "end": v(32, -1.99) * mm});
            skLineSegment(sketch, "E338", {"start": v(32, -1.99) * mm, "end": v(31.83, -1.9) * mm});
            skLineSegment(sketch, "E339", {"start": v(31.83, -1.9) * mm, "end": v(31.67, -1.83) * mm});
            skLineSegment(sketch, "E340", {"start": v(31.67, -1.83) * mm, "end": v(31.5, -1.76) * mm});
            skLineSegment(sketch, "E341", {"start": v(31.5, -1.76) * mm, "end": v(31.33, -1.7) * mm});
            skLineSegment(sketch, "E342", {"start": v(31.33, -1.7) * mm, "end": v(31.16, -1.63) * mm});
            skLineSegment(sketch, "E343", {"start": v(31.16, -1.63) * mm, "end": v(30.99, -1.58) * mm});
            skLineSegment(sketch, "E344", {"start": v(30.99, -1.58) * mm, "end": v(30.81, -1.53) * mm});
            skLineSegment(sketch, "E345", {"start": v(30.81, -1.53) * mm, "end": v(30.64, -1.48) * mm});
            skLineSegment(sketch, "E346", {"start": v(30.64, -1.48) * mm, "end": v(30.46, -1.44) * mm});
            skLineSegment(sketch, "E347", {"start": v(34.7, -4.59) * mm, "end": v(30, -8.28) * mm});
            skLineSegment(sketch, "E348", {"start": v(30, -8.28) * mm, "end": v(29.2, -14.2) * mm});
            skLineSegment(sketch, "E349", {"start": v(29.2, -14.2) * mm, "end": v(29.33, -14.19) * mm});
            skLineSegment(sketch, "E350", {"start": v(29.33, -14.19) * mm, "end": v(29.46, -14.18) * mm});
            skLineSegment(sketch, "E351", {"start": v(29.46, -14.18) * mm, "end": v(29.6, -14.17) * mm});
            skLineSegment(sketch, "E352", {"start": v(29.6, -14.17) * mm, "end": v(29.73, -14.16) * mm});
            skLineSegment(sketch, "E353", {"start": v(29.73, -14.16) * mm, "end": v(29.86, -14.14) * mm});
            skLineSegment(sketch, "E354", {"start": v(29.86, -14.14) * mm, "end": v(29.99, -14.12) * mm});
            skLineSegment(sketch, "E355", {"start": v(29.99, -14.12) * mm, "end": v(30.12, -14.1) * mm});
            skLineSegment(sketch, "E356", {"start": v(30.12, -14.1) * mm, "end": v(30.25, -14.08) * mm});
            skLineSegment(sketch, "E357", {"start": v(30.25, -14.08) * mm, "end": v(30.38, -14.05) * mm});
            skLineSegment(sketch, "E358", {"start": v(30.38, -14.05) * mm, "end": v(30.51, -14.03) * mm});
            skLineSegment(sketch, "E359", {"start": v(30.51, -14.03) * mm, "end": v(30.64, -14) * mm});
            skLineSegment(sketch, "E360", {"start": v(30.64, -14) * mm, "end": v(30.77, -13.96) * mm});
            skLineSegment(sketch, "E361", {"start": v(30.77, -13.96) * mm, "end": v(30.9, -13.92) * mm});
            skLineSegment(sketch, "E362", {"start": v(30.9, -13.92) * mm, "end": v(31.03, -13.88) * mm});
            skLineSegment(sketch, "E363", {"start": v(31.03, -13.88) * mm, "end": v(31.16, -13.84) * mm});
            skLineSegment(sketch, "E364", {"start": v(31.16, -13.84) * mm, "end": v(31.28, -13.8) * mm});
            skLineSegment(sketch, "E365", {"start": v(31.28, -13.8) * mm, "end": v(31.4, -13.75) * mm});
            skLineSegment(sketch, "E366", {"start": v(31.4, -13.75) * mm, "end": v(31.53, -13.7) * mm});
            skLineSegment(sketch, "E367", {"start": v(31.53, -13.7) * mm, "end": v(31.65, -13.65) * mm});
            skLineSegment(sketch, "E368", {"start": v(31.65, -13.65) * mm, "end": v(31.78, -13.6) * mm});
            skLineSegment(sketch, "E369", {"start": v(31.78, -13.6) * mm, "end": v(31.9, -13.54) * mm});
            skLineSegment(sketch, "E370", {"start": v(31.9, -13.54) * mm, "end": v(32.02, -13.48) * mm});
            skLineSegment(sketch, "E371", {"start": v(32.02, -13.48) * mm, "end": v(32.13, -13.42) * mm});
            skLineSegment(sketch, "E372", {"start": v(32.13, -13.42) * mm, "end": v(32.25, -13.35) * mm});
            skLineSegment(sketch, "E373", {"start": v(32.25, -13.35) * mm, "end": v(32.37, -13.29) * mm});
            skLineSegment(sketch, "E374", {"start": v(32.37, -13.29) * mm, "end": v(32.48, -13.22) * mm});
            skLineSegment(sketch, "E375", {"start": v(32.48, -13.22) * mm, "end": v(32.6, -13.14) * mm});
            skLineSegment(sketch, "E376", {"start": v(32.6, -13.14) * mm, "end": v(32.7, -13.07) * mm});
            skLineSegment(sketch, "E377", {"start": v(32.7, -13.07) * mm, "end": v(32.81, -13) * mm});
            skLineSegment(sketch, "E378", {"start": v(32.81, -13) * mm, "end": v(32.91, -12.92) * mm});
            skLineSegment(sketch, "E379", {"start": v(32.91, -12.92) * mm, "end": v(33.01, -12.84) * mm});
            skLineSegment(sketch, "E380", {"start": v(33.01, -12.84) * mm, "end": v(33.11, -12.77) * mm});
            skLineSegment(sketch, "E381", {"start": v(33.11, -12.77) * mm, "end": v(33.2, -12.69) * mm});
            skLineSegment(sketch, "E382", {"start": v(33.2, -12.69) * mm, "end": v(33.3, -12.6) * mm});
            skLineSegment(sketch, "E383", {"start": v(33.3, -12.6) * mm, "end": v(33.4, -12.52) * mm});
            skLineSegment(sketch, "E384", {"start": v(33.4, -12.52) * mm, "end": v(33.5, -12.44) * mm});
            skLineSegment(sketch, "E385", {"start": v(33.5, -12.44) * mm, "end": v(33.58, -12.35) * mm});
            skLineSegment(sketch, "E386", {"start": v(33.58, -12.35) * mm, "end": v(33.67, -12.26) * mm});
            skLineSegment(sketch, "E387", {"start": v(33.67, -12.26) * mm, "end": v(33.76, -12.17) * mm});
            skLineSegment(sketch, "E388", {"start": v(33.76, -12.17) * mm, "end": v(33.84, -12.08) * mm});
            skLineSegment(sketch, "E389", {"start": v(33.84, -12.08) * mm, "end": v(33.92, -11.99) * mm});
            skLineSegment(sketch, "E390", {"start": v(33.92, -11.99) * mm, "end": v(34, -11.9) * mm});
            skLineSegment(sketch, "E391", {"start": v(34, -11.9) * mm, "end": v(34.09, -11.8) * mm});
            skLineSegment(sketch, "E392", {"start": v(34.09, -11.8) * mm, "end": v(34.16, -11.7) * mm});
            skLineSegment(sketch, "E393", {"start": v(34.16, -11.7) * mm, "end": v(34.24, -11.6) * mm});
            skLineSegment(sketch, "E394", {"start": v(34.24, -11.6) * mm, "end": v(34.31, -11.5) * mm});
            skLineSegment(sketch, "E395", {"start": v(34.31, -11.5) * mm, "end": v(34.38, -11.4) * mm});
            skLineSegment(sketch, "E396", {"start": v(34.38, -11.4) * mm, "end": v(34.45, -11.29) * mm});
            skLineSegment(sketch, "E397", {"start": v(34.45, -11.29) * mm, "end": v(34.52, -11.18) * mm});
            skLineSegment(sketch, "E398", {"start": v(34.52, -11.18) * mm, "end": v(34.59, -11.08) * mm});
            skLineSegment(sketch, "E399", {"start": v(34.59, -11.08) * mm, "end": v(34.65, -10.97) * mm});
            skLineSegment(sketch, "E400", {"start": v(34.65, -10.97) * mm, "end": v(34.71, -10.86) * mm});
            skLineSegment(sketch, "E401", {"start": v(34.71, -10.86) * mm, "end": v(34.77, -10.75) * mm});
            skLineSegment(sketch, "E402", {"start": v(34.77, -10.75) * mm, "end": v(34.83, -10.64) * mm});
            skLineSegment(sketch, "E403", {"start": v(34.83, -10.64) * mm, "end": v(34.89, -10.53) * mm});
            skLineSegment(sketch, "E404", {"start": v(34.89, -10.53) * mm, "end": v(34.94, -10.41) * mm});
            skLineSegment(sketch, "E405", {"start": v(34.94, -10.41) * mm, "end": v(34.99, -10.3) * mm});
            skLineSegment(sketch, "E406", {"start": v(34.99, -10.3) * mm, "end": v(35.04, -10.18) * mm});
            skLineSegment(sketch, "E407", {"start": v(35.04, -10.18) * mm, "end": v(35.43, -8.84) * mm});
            skLineSegment(sketch, "E408", {"start": v(35.43, -8.84) * mm, "end": v(35.45, -8.69) * mm});
            skLineSegment(sketch, "E409", {"start": v(35.45, -8.69) * mm, "end": v(35.47, -8.54) * mm});
            skLineSegment(sketch, "E410", {"start": v(35.47, -8.54) * mm, "end": v(35.49, -8.39) * mm});
            skLineSegment(sketch, "E411", {"start": v(35.49, -8.39) * mm, "end": v(35.5, -8.24) * mm});
            skLineSegment(sketch, "E412", {"start": v(35.5, -8.24) * mm, "end": v(35.51, -8.08) * mm});
            skLineSegment(sketch, "E413", {"start": v(35.51, -8.08) * mm, "end": v(35.52, -7.93) * mm});
            skLineSegment(sketch, "E414", {"start": v(35.52, -7.93) * mm, "end": v(35.52, -7.78) * mm});
            skLineSegment(sketch, "E415", {"start": v(35.52, -7.78) * mm, "end": v(35.52, -7.63) * mm});
            skLineSegment(sketch, "E416", {"start": v(35.52, -7.63) * mm, "end": v(35.52, -7.48) * mm});
            skLineSegment(sketch, "E417", {"start": v(35.52, -7.48) * mm, "end": v(35.5, -7.33) * mm});
            skLineSegment(sketch, "E418", {"start": v(35.5, -7.33) * mm, "end": v(35.5, -7.18) * mm});
            skLineSegment(sketch, "E419", {"start": v(35.5, -7.18) * mm, "end": v(35.48, -7.03) * mm});
            skLineSegment(sketch, "E420", {"start": v(35.48, -7.03) * mm, "end": v(35.46, -6.88) * mm});
            skLineSegment(sketch, "E421", {"start": v(35.46, -6.88) * mm, "end": v(35.44, -6.73) * mm});
            skLineSegment(sketch, "E422", {"start": v(35.44, -6.73) * mm, "end": v(35.42, -6.58) * mm});
            skLineSegment(sketch, "E423", {"start": v(35.42, -6.58) * mm, "end": v(35.39, -6.43) * mm});
            skLineSegment(sketch, "E424", {"start": v(35.39, -6.43) * mm, "end": v(35.36, -6.28) * mm});
            skLineSegment(sketch, "E425", {"start": v(35.36, -6.28) * mm, "end": v(35.32, -6.13) * mm});
            skLineSegment(sketch, "E426", {"start": v(35.32, -6.13) * mm, "end": v(35.28, -5.99) * mm});
            skLineSegment(sketch, "E427", {"start": v(35.28, -5.99) * mm, "end": v(35.24, -5.84) * mm});
            skLineSegment(sketch, "E428", {"start": v(35.24, -5.84) * mm, "end": v(35.2, -5.7) * mm});
            skLineSegment(sketch, "E429", {"start": v(35.2, -5.7) * mm, "end": v(35.14, -5.55) * mm});
            skLineSegment(sketch, "E430", {"start": v(35.14, -5.55) * mm, "end": v(35.1, -5.41) * mm});
            skLineSegment(sketch, "E431", {"start": v(35.1, -5.41) * mm, "end": v(35.03, -5.27) * mm});
            skLineSegment(sketch, "E432", {"start": v(35.03, -5.27) * mm, "end": v(34.98, -5.13) * mm});
            skLineSegment(sketch, "E433", {"start": v(34.98, -5.13) * mm, "end": v(34.91, -5) * mm});
            skLineSegment(sketch, "E434", {"start": v(34.91, -5) * mm, "end": v(34.85, -4.86) * mm});
            skLineSegment(sketch, "E435", {"start": v(34.85, -4.86) * mm, "end": v(34.78, -4.72) * mm});
            skLineSegment(sketch, "E436", {"start": v(34.78, -4.72) * mm, "end": v(34.7, -4.59) * mm});
            skLineSegment(sketch, "E437", {"start": v(23.44, -4.6) * mm, "end": v(23.36, -4.74) * mm});
            skLineSegment(sketch, "E438", {"start": v(23.36, -4.74) * mm, "end": v(23.28, -4.88) * mm});
            skLineSegment(sketch, "E439", {"start": v(23.28, -4.88) * mm, "end": v(23.21, -5.03) * mm});
            skLineSegment(sketch, "E440", {"start": v(23.21, -5.03) * mm, "end": v(23.15, -5.18) * mm});
            skLineSegment(sketch, "E441", {"start": v(23.15, -5.18) * mm, "end": v(23.08, -5.33) * mm});
            skLineSegment(sketch, "E442", {"start": v(23.08, -5.33) * mm, "end": v(23.02, -5.49) * mm});
            skLineSegment(sketch, "E443", {"start": v(23.02, -5.49) * mm, "end": v(22.97, -5.64) * mm});
            skLineSegment(sketch, "E444", {"start": v(22.97, -5.64) * mm, "end": v(22.92, -5.8) * mm});
            skLineSegment(sketch, "E445", {"start": v(22.92, -5.8) * mm, "end": v(22.87, -5.96) * mm});
            skLineSegment(sketch, "E446", {"start": v(22.87, -5.96) * mm, "end": v(22.83, -6.11) * mm});
            skLineSegment(sketch, "E447", {"start": v(22.83, -6.11) * mm, "end": v(22.79, -6.27) * mm});
            skLineSegment(sketch, "E448", {"start": v(22.79, -6.27) * mm, "end": v(22.75, -6.43) * mm});
            skLineSegment(sketch, "E449", {"start": v(22.75, -6.43) * mm, "end": v(22.72, -6.6) * mm});
            skLineSegment(sketch, "E450", {"start": v(22.72, -6.6) * mm, "end": v(22.7, -6.76) * mm});
            skLineSegment(sketch, "E451", {"start": v(22.7, -6.76) * mm, "end": v(22.67, -6.92) * mm});
            skLineSegment(sketch, "E452", {"start": v(22.67, -6.92) * mm, "end": v(22.65, -7.08) * mm});
            skLineSegment(sketch, "E453", {"start": v(22.65, -7.08) * mm, "end": v(22.64, -7.25) * mm});
            skLineSegment(sketch, "E454", {"start": v(22.64, -7.25) * mm, "end": v(22.63, -7.41) * mm});
            skLineSegment(sketch, "E455", {"start": v(22.63, -7.41) * mm, "end": v(22.62, -7.58) * mm});
            skLineSegment(sketch, "E456", {"start": v(22.62, -7.58) * mm, "end": v(22.62, -7.74) * mm});
            skLineSegment(sketch, "E457", {"start": v(22.62, -7.74) * mm, "end": v(22.62, -7.9) * mm});
            skLineSegment(sketch, "E458", {"start": v(22.62, -7.9) * mm, "end": v(22.63, -8.07) * mm});
            skLineSegment(sketch, "E459", {"start": v(22.63, -8.07) * mm, "end": v(22.64, -8.23) * mm});
            skLineSegment(sketch, "E460", {"start": v(22.64, -8.23) * mm, "end": v(22.65, -8.4) * mm});
            skLineSegment(sketch, "E461", {"start": v(22.65, -8.4) * mm, "end": v(22.67, -8.56) * mm});
            skLineSegment(sketch, "E462", {"start": v(22.67, -8.56) * mm, "end": v(22.7, -8.72) * mm});
            skLineSegment(sketch, "E463", {"start": v(22.7, -8.72) * mm, "end": v(22.72, -8.88) * mm});
            skLineSegment(sketch, "E464", {"start": v(22.72, -8.88) * mm, "end": v(22.75, -9.05) * mm});
            skLineSegment(sketch, "E465", {"start": v(22.75, -9.05) * mm, "end": v(22.79, -9.2) * mm});
            skLineSegment(sketch, "E466", {"start": v(22.79, -9.2) * mm, "end": v(22.82, -9.35) * mm});
            skLineSegment(sketch, "E467", {"start": v(22.82, -9.35) * mm, "end": v(22.86, -9.48) * mm});
            skLineSegment(sketch, "E468", {"start": v(22.86, -9.48) * mm, "end": v(22.9, -9.62) * mm});
            skLineSegment(sketch, "E469", {"start": v(22.9, -9.62) * mm, "end": v(22.94, -9.76) * mm});
            skLineSegment(sketch, "E470", {"start": v(22.94, -9.76) * mm, "end": v(23, -9.9) * mm});
            skLineSegment(sketch, "E471", {"start": v(23, -9.9) * mm, "end": v(23.04, -10.03) * mm});
            skLineSegment(sketch, "E472", {"start": v(23.04, -10.03) * mm, "end": v(23.1, -10.16) * mm});
            skLineSegment(sketch, "E473", {"start": v(23.1, -10.16) * mm, "end": v(23.15, -10.29) * mm});
            skLineSegment(sketch, "E474", {"start": v(23.15, -10.29) * mm, "end": v(23.2, -10.42) * mm});
            skLineSegment(sketch, "E475", {"start": v(23.2, -10.42) * mm, "end": v(23.27, -10.55) * mm});
            skLineSegment(sketch, "E476", {"start": v(23.27, -10.55) * mm, "end": v(23.33, -10.68) * mm});
            skLineSegment(sketch, "E477", {"start": v(23.33, -10.68) * mm, "end": v(23.4, -10.8) * mm});
            skLineSegment(sketch, "E478", {"start": v(23.4, -10.8) * mm, "end": v(23.46, -10.93) * mm});
            skLineSegment(sketch, "E479", {"start": v(23.46, -10.93) * mm, "end": v(23.54, -11.05) * mm});
            skLineSegment(sketch, "E480", {"start": v(23.54, -11.05) * mm, "end": v(23.61, -11.17) * mm});
            skLineSegment(sketch, "E481", {"start": v(23.61, -11.17) * mm, "end": v(23.69, -11.3) * mm});
            skLineSegment(sketch, "E482", {"start": v(23.69, -11.3) * mm, "end": v(23.77, -11.41) * mm});
            skLineSegment(sketch, "E483", {"start": v(23.77, -11.41) * mm, "end": v(23.85, -11.53) * mm});
            skLineSegment(sketch, "E484", {"start": v(23.85, -11.53) * mm, "end": v(23.94, -11.64) * mm});
            skLineSegment(sketch, "E485", {"start": v(23.94, -11.64) * mm, "end": v(24.02, -11.76) * mm});
            skLineSegment(sketch, "E486", {"start": v(24.02, -11.76) * mm, "end": v(24.11, -11.87) * mm});
            skLineSegment(sketch, "E487", {"start": v(24.11, -11.87) * mm, "end": v(24.2, -11.98) * mm});
            skLineSegment(sketch, "E488", {"start": v(24.2, -11.98) * mm, "end": v(24.3, -12.08) * mm});
            skLineSegment(sketch, "E489", {"start": v(24.3, -12.08) * mm, "end": v(24.4, -12.19) * mm});
            skLineSegment(sketch, "E490", {"start": v(24.4, -12.19) * mm, "end": v(24.5, -12.29) * mm});
            skLineSegment(sketch, "E491", {"start": v(24.5, -12.29) * mm, "end": v(24.6, -12.39) * mm});
            skLineSegment(sketch, "E492", {"start": v(24.6, -12.39) * mm, "end": v(24.7, -12.49) * mm});
            skLineSegment(sketch, "E493", {"start": v(24.7, -12.49) * mm, "end": v(24.8, -12.58) * mm});
            skLineSegment(sketch, "E494", {"start": v(24.8, -12.58) * mm, "end": v(24.92, -12.68) * mm});
            skLineSegment(sketch, "E495", {"start": v(24.92, -12.68) * mm, "end": v(25.04, -12.77) * mm});
            skLineSegment(sketch, "E496", {"start": v(25.04, -12.77) * mm, "end": v(25.16, -12.87) * mm});
            skLineSegment(sketch, "E497", {"start": v(25.16, -12.87) * mm, "end": v(25.28, -12.96) * mm});
            skLineSegment(sketch, "E498", {"start": v(25.28, -12.96) * mm, "end": v(25.4, -13.05) * mm});
            skLineSegment(sketch, "E499", {"start": v(25.4, -13.05) * mm, "end": v(25.53, -13.14) * mm});
            skLineSegment(sketch, "E500", {"start": v(25.53, -13.14) * mm, "end": v(25.66, -13.22) * mm});
            skLineSegment(sketch, "E501", {"start": v(25.66, -13.22) * mm, "end": v(25.8, -13.3) * mm});
            skLineSegment(sketch, "E502", {"start": v(25.8, -13.3) * mm, "end": v(25.93, -13.38) * mm});
            skLineSegment(sketch, "E503", {"start": v(25.93, -13.38) * mm, "end": v(26.06, -13.45) * mm});
            skLineSegment(sketch, "E504", {"start": v(26.06, -13.45) * mm, "end": v(26.2, -13.52) * mm});
            skLineSegment(sketch, "E505", {"start": v(26.2, -13.52) * mm, "end": v(26.34, -13.58) * mm});
            skLineSegment(sketch, "E506", {"start": v(26.34, -13.58) * mm, "end": v(26.48, -13.65) * mm});
            skLineSegment(sketch, "E507", {"start": v(26.48, -13.65) * mm, "end": v(26.62, -13.7) * mm});
            skLineSegment(sketch, "E508", {"start": v(26.62, -13.7) * mm, "end": v(26.76, -13.76) * mm});
            skLineSegment(sketch, "E509", {"start": v(26.76, -13.76) * mm, "end": v(26.9, -13.82) * mm});
            skLineSegment(sketch, "E510", {"start": v(26.9, -13.82) * mm, "end": v(27.05, -13.87) * mm});
            skLineSegment(sketch, "E511", {"start": v(27.05, -13.87) * mm, "end": v(27.2, -13.91) * mm});
            skLineSegment(sketch, "E512", {"start": v(27.2, -13.91) * mm, "end": v(27.35, -13.96) * mm});
            skLineSegment(sketch, "E513", {"start": v(27.35, -13.96) * mm, "end": v(27.5, -14) * mm});
            skLineSegment(sketch, "E514", {"start": v(27.5, -14) * mm, "end": v(27.65, -14.03) * mm});
            skLineSegment(sketch, "E515", {"start": v(27.65, -14.03) * mm, "end": v(27.8, -14.06) * mm});
            skLineSegment(sketch, "E516", {"start": v(27.8, -14.06) * mm, "end": v(27.95, -14.1) * mm});
            skLineSegment(sketch, "E517", {"start": v(27.95, -14.1) * mm, "end": v(28.1, -14.12) * mm});
            skLineSegment(sketch, "E518", {"start": v(28.1, -14.12) * mm, "end": v(28.25, -14.14) * mm});
            skLineSegment(sketch, "E519", {"start": v(28.25, -14.14) * mm, "end": v(28.4, -14.16) * mm});
            skLineSegment(sketch, "E520", {"start": v(28.4, -14.16) * mm, "end": v(28.56, -14.17) * mm});
            skLineSegment(sketch, "E521", {"start": v(28.56, -14.17) * mm, "end": v(28.71, -14.18) * mm});
            skLineSegment(sketch, "E522", {"start": v(28.71, -14.18) * mm, "end": v(28.87, -14.19) * mm});
            skLineSegment(sketch, "E523", {"start": v(28.87, -14.19) * mm, "end": v(29.02, -14.2) * mm});
            skLineSegment(sketch, "E524", {"start": v(29.02, -14.2) * mm, "end": v(28.2, -8.25) * mm});
            skLineSegment(sketch, "E525", {"start": v(28.2, -8.25) * mm, "end": v(23.44, -4.6) * mm});
            skText(sketch, "E526", { "text": "John\nSmith", "fontName": "OpenSans-Regular.ttf"});
            const initialGuessF4  = {"E526": [0.0208, -0.01005, -1, 0, 0.005]};
            skSetInitialGuess(sketch, initialGuessF4);
            skSolve(sketch);
        }
        {
            var Q0;
            Q0 = qSketchRegion(id + "F4", true);
            extrude(context, id + "F5", {"entities" : qUnion([Q0]), "operationType" : NewBodyOperationType.REMOVE, "oppositeDirection" : true, "depth" : 1 * mm, "offsetDistance" : 25 * mm});
        }
        {
            var Q0;
            {var subQ0=sQuery(id+"F0.wireOp",EDGE,"E4.filletArc");var subQ1=sQuery(id+"F0.wireOp",EDGE,"E1.filletArc");var subQ2=sQuery(id+"F0.wireOp",EDGE,"E0.right");var subQ3=sQuery(id+"F0.wireOp",EDGE,"E0.left");var subQ4=sQuery(id+"F0.wireOp",EDGE,"E0.top");var subQ5=sQuery(id+"F0.wireOp",EDGE,"E0.bottom");var subQ6=sQuery(id+"F0.wireOp",EDGE,"E2.filletArc");var subQ7=sQuery(id+"F0.wireOp",EDGE,"E3.filletArc");Q0=makeQuery(id+"F5.boolean.opBoolean","SPLIT",FACE,{"disambiguationData":[TD([makeQuery(id+"F1.opExtrude","SWEPT_FACE",FACE,{"disambiguationData":[OSD([subQ5])]})])],"derivedFrom":makeQuery(id+"F1.opExtrude","CAP_FACE",FACE,{"disambiguationData":[OSD([subQ5,subQ4,subQ3,subQ2,subQ1,subQ6,subQ7,subQ0])],"isStart":true})});}
            var sketch = newSketch(context, id + "F6", { "sketchPlane" : qUnion([Q0])});
            skLineSegment(sketch, "E527", {"start": v(19, -16) * mm, "end": v(19, 0) * mm, "construction": true});
            skLineSegment(sketch, "E528", {"start": v(34.47, -14.69) * mm, "end": v(32.47, -14.69) * mm});
            skArc(sketch, "E529.0.startCap", {"start": v(34.47, -14.19) * mm, "mid": v(34.97, -14.69) * mm, "end": v(34.47, -15.19) * mm});
            skArc(sketch, "E529.0.endCap", {"start": v(32.47, -15.19) * mm, "mid": v(31.97, -14.69) * mm, "end": v(32.47, -14.19) * mm});
            skLineSegment(sketch, "E529.0.left", {"start": v(34.47, -15.19) * mm, "end": v(32.47, -15.19) * mm});
            skLineSegment(sketch, "E529.0.right", {"start": v(34.47, -14.19) * mm, "end": v(32.47, -14.19) * mm});
            skArc(sketch, "E530.MirrorCS", {"start": v(5.53, -15.19) * mm, "mid": v(6.03, -14.69) * mm, "end": v(5.53, -14.19) * mm});
            skLineSegment(sketch, "E531.MirrorCS", {"start": v(3.53, -15.19) * mm, "end": v(5.53, -15.19) * mm});
            skLineSegment(sketch, "E532.MirrorCS", {"start": v(3.53, -14.19) * mm, "end": v(5.53, -14.19) * mm});
            skArc(sketch, "E533.MirrorCS", {"start": v(3.53, -14.19) * mm, "mid": v(3.03, -14.69) * mm, "end": v(3.53, -15.19) * mm});
            skSolve(sketch);
        }
        {
            var Q0;
            Q0 = qSketchRegion(id + "F6", true);
            extrude(context, id + "F7", {"entities" : qUnion([Q0]), "operationType" : NewBodyOperationType.REMOVE, "endBound" : BoundingType.THROUGH_ALL, "oppositeDirection" : true, "depth" : 25 * mm, "offsetDistance" : 25 * mm});
        }
    });
